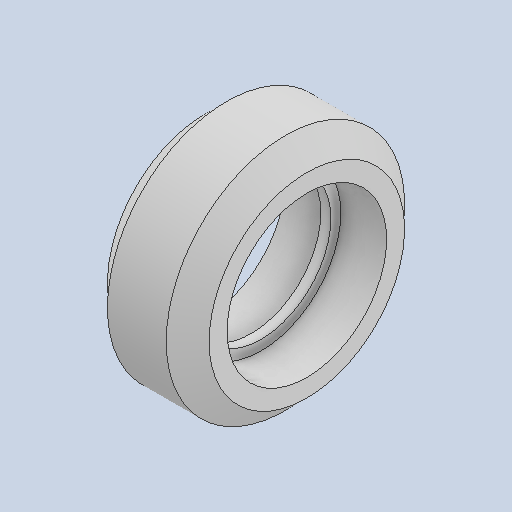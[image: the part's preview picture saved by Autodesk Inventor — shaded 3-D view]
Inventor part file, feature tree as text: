
AUTODESK INVENTOR PART (.ipt)
format: ipt  version: 2023.1 (Build 271208000, 208)  size: 140,288 bytes
history: native  units: mm
features: revolve x1
ambient origin geometry x8: Origin, YZ Plane, XZ Plane, XY Plane, X Axis, Y Axis, Z Axis, Center Point
bodies: Solid1 (feature_tree)
feature tree (1):
  revolve  "Revolve1"  [1 undecoded]
note: 1 required parameter value undecoded (feature->parameter linkage not recoverable at this tier; creation-order binding heuristic only, values carry confidence <= 0.55)
